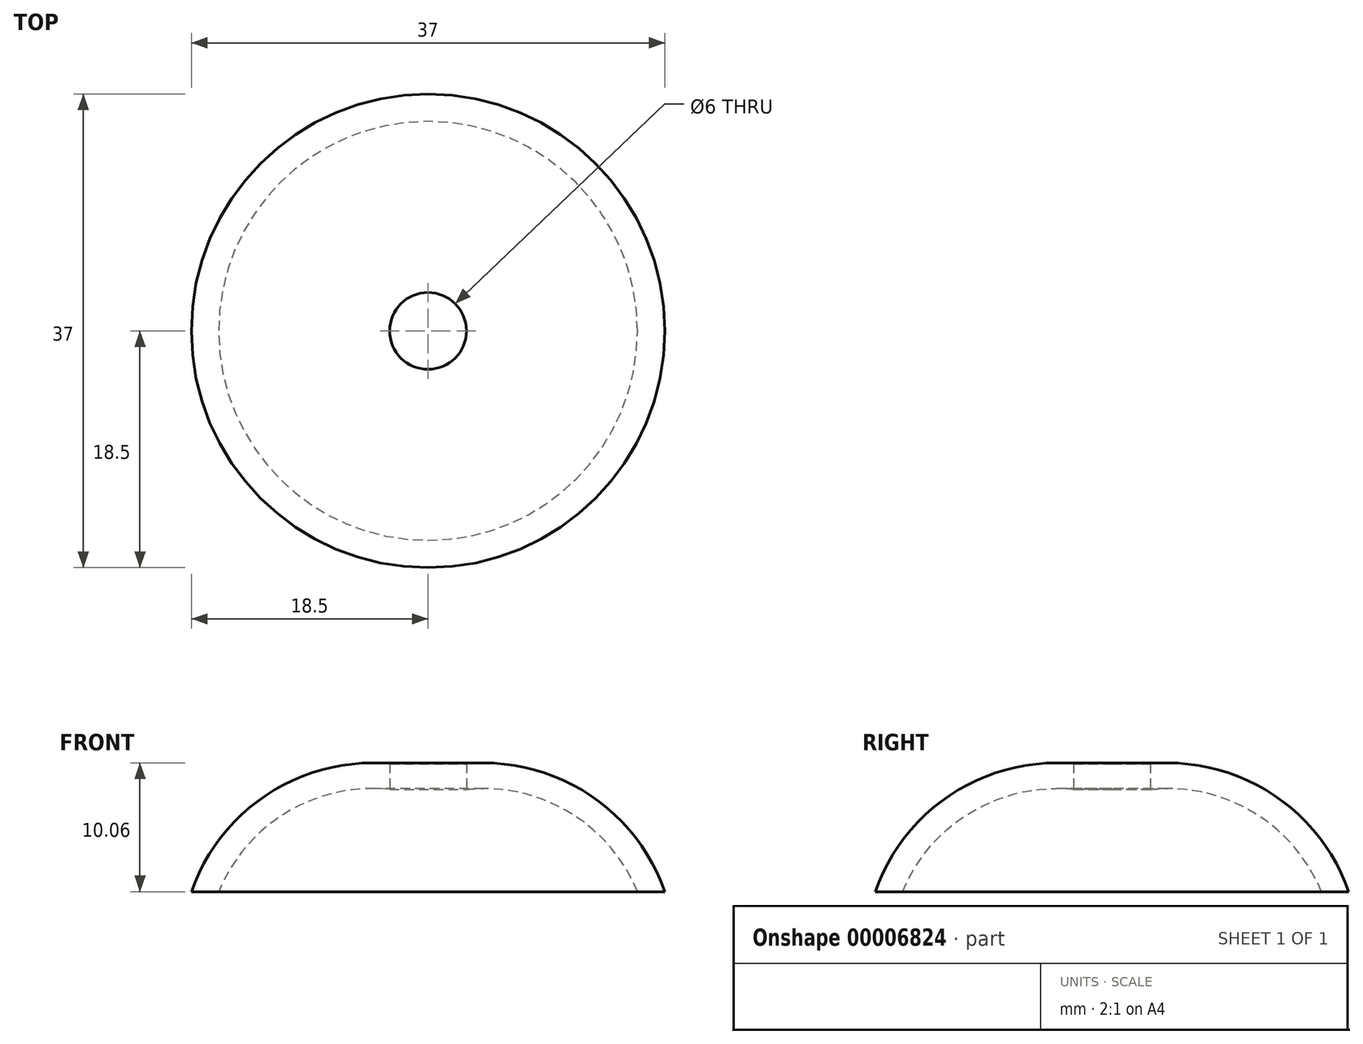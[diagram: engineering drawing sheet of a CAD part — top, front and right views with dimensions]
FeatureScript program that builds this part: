
annotation { "Feature Type Name" : "Feature", "Feature Type Description" : "" }
export const myFeature = defineFeature(function(context is Context, id is Id, definition is map)
    precondition{}
    {
        {
            var Q0;
            Q0=qCreatedBy(makeId("Right.planeOp"),FACE);
            var sketch = newSketch(context, id + "F0", { "sketchPlane" : qUnion([Q0])});
            skLineSegment(sketch, "E0", {"start": v(0, 0) * mm, "end": v(0, -3.09) * mm});
            skLineSegment(sketch, "E1", {"start": v(4.26, -9.53) * mm, "end": v(36, -23) * mm});
            skLineSegment(sketch, "E2", {"start": v(36, -23) * mm, "end": v(70, -23) * mm});
            skLineSegment(sketch, "E3", {"start": v(90, -3) * mm, "end": v(90, 47) * mm});
            skLineSegment(sketch, "E4", {"start": v(70, 67) * mm, "end": v(7, 67) * mm});
            skLineSegment(sketch, "E5", {"start": v(7, 67) * mm, "end": v(7, 45) * mm});
            skLineSegment(sketch, "E6", {"start": v(7, 45) * mm, "end": v(61, 45) * mm});
            skLineSegment(sketch, "E7", {"start": v(68, 38) * mm, "end": v(68, 4) * mm});
            skLineSegment(sketch, "E8", {"start": v(61, -3) * mm, "end": v(36, -3) * mm});
            skLineSegment(sketch, "E9", {"start": v(36, -3) * mm, "end": v(36, 0) * mm});
            skLineSegment(sketch, "E10", {"start": v(36, 0) * mm, "end": v(0, 0) * mm});
            skLineSegment(sketch, "E11", {"start": v(36, -23) * mm, "end": v(21.85, -23) * mm, "construction": true});
            skPoint(sketch, "E12.visualSharp", {"position": v(90, -23) * mm});
            skArc(sketch, "E12.filletArc", {"start": v(70, -23) * mm, "mid": v(84.14, -17.14) * mm, "end": v(90, -3) * mm});
            skPoint(sketch, "E13.visualSharp", {"position": v(90, 67) * mm});
            skArc(sketch, "E13.filletArc", {"start": v(90, 47) * mm, "mid": v(84.14, 61.14) * mm, "end": v(70, 67) * mm});
            skPoint(sketch, "E14.visualSharp", {"position": v(68, 45) * mm});
            skArc(sketch, "E14.filletArc", {"start": v(68, 38) * mm, "mid": v(65.95, 42.95) * mm, "end": v(61, 45) * mm});
            skPoint(sketch, "E15.visualSharp", {"position": v(68, -3) * mm});
            skArc(sketch, "E15.filletArc", {"start": v(61, -3) * mm, "mid": v(65.95, -0.95) * mm, "end": v(68, 4) * mm});
            skPoint(sketch, "E16.visualSharp", {"position": v(0, -7.72) * mm});
            skArc(sketch, "E16.filletArc", {"start": v(0, -3.09) * mm, "mid": v(1.16, -6.95) * mm, "end": v(4.26, -9.53) * mm});
            skSolve(sketch);
        }
        {
            var Q0;
            Q0=qSketchRegion(id+"F0",true);
            extrude(context, id + "F1", {"entities" : qUnion([Q0]), "endBound" : BoundingType.SYMMETRIC, "depth" : 20 * mm});
        }
        {
            var Q0;
            Q0=makeQuery(id+"F1.opExtrude","SWEPT_FACE",FACE,{"disambiguationData":[OSD([sQuery(id+"F0.wireOp",EDGE,"E6")])]});
            var sketch = newSketch(context, id + "F2", { "sketchPlane" : qUnion([Q0])});
            skCircle(sketch, "E17", {"center": v(0, -18) * mm, "radius": 11 * mm});
            skCircle(sketch, "E18", {"center": v(0, -18) * mm, "radius": 7 * mm});
            skSolve(sketch);
        }
        {
            var Q0;
            Q0=qSketchRegion(id+"F2",true);
            extrude(context, id + "F3", {"entities" : qUnion([Q0]), "operationType" : NewBodyOperationType.ADD, "oppositeDirection" : true, "depth" : 25 * mm});
        }
        {
            var Q0;
            Q0=makeQuery(id+"F3.boolean.opBoolean","SPLIT",FACE,{"disambiguationData":[TD([makeQuery(id+"F3.opExtrude","SWEPT_FACE",FACE,{"disambiguationData":[OSD([sQuery(id+"F2.wireOp",EDGE,"E18")])]})])],"derivedFrom":makeQuery(id+"F1.opExtrude","SWEPT_FACE",FACE,{"disambiguationData":[OSD([sQuery(id+"F0.wireOp",EDGE,"E4")])]})});
            var sketch = newSketch(context, id + "F4", { "sketchPlane" : qUnion([Q0])});
            skCircle(sketch, "E19.0", {"center": v(0, 18) * mm, "radius": 7 * mm});
            skSolve(sketch);
        }
        {
            var Q0;
            Q0=qSketchRegion(id+"F4",true);
            extrude(context, id + "F5", {"entities" : qUnion([Q0]), "operationType" : NewBodyOperationType.REMOVE, "oppositeDirection" : true, "depth" : 25 * mm});
        }
        {
            var Q0;
            {var subQ0=sQuery(id+"F0.wireOp",EDGE,"E4");var subQ1=makeQuery(id+"F1.opExtrude","SWEPT_FACE",FACE,{"disambiguationData":[OSD([subQ0])]});var subQ2=sQuery(id+"F0.wireOp",EDGE,"E5");Q0=makeQuery(id+"F3.boolean.opBoolean","SPLIT",FACE,{"disambiguationData":[TD([makeQuery(id+"F1.opExtrude","CAP_FACE",FACE,{"disambiguationData":[OSD([sQuery(id+"F0.wireOp",EDGE,"E0"),sQuery(id+"F0.wireOp",EDGE,"E1"),sQuery(id+"F0.wireOp",EDGE,"E2"),sQuery(id+"F0.wireOp",EDGE,"E3"),subQ0,subQ2,sQuery(id+"F0.wireOp",EDGE,"E6"),sQuery(id+"F0.wireOp",EDGE,"E7"),sQuery(id+"F0.wireOp",EDGE,"E8"),sQuery(id+"F0.wireOp",EDGE,"E9"),sQuery(id+"F0.wireOp",EDGE,"E10"),sQuery(id+"F0.wireOp",EDGE,"E12.filletArc"),sQuery(id+"F0.wireOp",EDGE,"E13.filletArc"),sQuery(id+"F0.wireOp",EDGE,"E14.filletArc"),sQuery(id+"F0.wireOp",EDGE,"E15.filletArc"),sQuery(id+"F0.wireOp",EDGE,"E16.filletArc")])],"isStart":false}),subQ1,makeQuery(id+"F1.opExtrude","SWEPT_FACE",FACE,{"disambiguationData":[OSD([subQ2])]}),makeQuery(id+"F3.opExtrude","SWEPT_FACE",FACE,{"disambiguationData":[OSD([sQuery(id+"F2.wireOp",EDGE,"E17")])]})])],"derivedFrom":subQ1});}
            var sketch = newSketch(context, id + "F6", { "sketchPlane" : qUnion([Q0])});
            skLineSegment(sketch, "E20.1.0", {"start": v(-10, 7) * mm, "end": v(0, 7) * mm});
            skArc(sketch, "E20.1.1", {"start": v(0, 7) * mm, "mid": v(-5.94, 8.74) * mm, "end": v(-10, 13.42) * mm});
            skLineSegment(sketch, "E20.1.2", {"start": v(-10, 13.42) * mm, "end": v(-10, 7) * mm});
            skSolve(sketch);
        }
        {
            var Q0;
            Q0=qSketchRegion(id+"F6",true);
            extrude(context, id + "F7", {"entities" : qUnion([Q0]), "operationType" : NewBodyOperationType.REMOVE, "oppositeDirection" : true, "depth" : 25 * mm});
        }
        {
            var Q0;
            {var subQ0=sQuery(id+"F0.wireOp",EDGE,"E4");var subQ1=makeQuery(id+"F1.opExtrude","SWEPT_FACE",FACE,{"disambiguationData":[OSD([subQ0])]});var subQ2=sQuery(id+"F0.wireOp",EDGE,"E5");Q0=makeQuery(id+"F3.boolean.opBoolean","SPLIT",FACE,{"disambiguationData":[TD([makeQuery(id+"F1.opExtrude","CAP_FACE",FACE,{"disambiguationData":[OSD([sQuery(id+"F0.wireOp",EDGE,"E0"),sQuery(id+"F0.wireOp",EDGE,"E1"),sQuery(id+"F0.wireOp",EDGE,"E2"),sQuery(id+"F0.wireOp",EDGE,"E3"),subQ0,subQ2,sQuery(id+"F0.wireOp",EDGE,"E6"),sQuery(id+"F0.wireOp",EDGE,"E7"),sQuery(id+"F0.wireOp",EDGE,"E8"),sQuery(id+"F0.wireOp",EDGE,"E9"),sQuery(id+"F0.wireOp",EDGE,"E10"),sQuery(id+"F0.wireOp",EDGE,"E12.filletArc"),sQuery(id+"F0.wireOp",EDGE,"E13.filletArc"),sQuery(id+"F0.wireOp",EDGE,"E14.filletArc"),sQuery(id+"F0.wireOp",EDGE,"E15.filletArc"),sQuery(id+"F0.wireOp",EDGE,"E16.filletArc")])],"isStart":false}),subQ1,makeQuery(id+"F1.opExtrude","SWEPT_FACE",FACE,{"disambiguationData":[OSD([subQ2])]}),makeQuery(id+"F3.opExtrude","SWEPT_FACE",FACE,{"disambiguationData":[OSD([sQuery(id+"F2.wireOp",EDGE,"E17")])]})])],"derivedFrom":subQ1});}
            var sketch = newSketch(context, id + "F8", { "sketchPlane" : qUnion([Q0])});
            skArc(sketch, "E21.0", {"start": v(10, 13.42) * mm, "mid": v(5.94, 8.74) * mm, "end": v(0, 7) * mm});
            skLineSegment(sketch, "E22", {"start": v(10, 13.42) * mm, "end": v(10, 7) * mm});
            skLineSegment(sketch, "E23", {"start": v(10, 7) * mm, "end": v(0, 7) * mm});
            skSolve(sketch);
        }
        {
            var Q0;
            Q0=qSketchRegion(id+"F8",true);
            extrude(context, id + "F9", {"entities" : qUnion([Q0]), "operationType" : NewBodyOperationType.REMOVE, "oppositeDirection" : true, "depth" : 25 * mm});
        }
        {
            var Q0;
            Q0=makeQuery(id+"F1.opExtrude","SWEPT_EDGE",EDGE,{"disambiguationData":[OSD([sQuery(id+"F0.wireOp",EDGE,"E8"),sQuery(id+"F0.wireOp",EDGE,"E9")])]});
            fillet(context, id + "F10", {"entities" : qUnion([Q0]), "radius" : 3 * mm, "tangentPropagation" : true, "allowEdgeOverflow" : false});
        }
        {
            var Q0;
            Q0=qCreatedBy(makeId("Right.planeOp"),FACE);
            var sketch = newSketch(context, id + "F11", { "sketchPlane" : qUnion([Q0])});
            skLineSegment(sketch, "E24", {"start": v(11, 100) * mm, "end": v(7, 100) * mm});
            skLineSegment(sketch, "E25", {"start": v(7, 100) * mm, "end": v(7, 118) * mm});
            skLineSegment(sketch, "E26", {"start": v(7, 118) * mm, "end": v(18, 118) * mm});
            skLineSegment(sketch, "E27", {"start": v(18, 118) * mm, "end": v(18, 35) * mm});
            skLineSegment(sketch, "E28", {"start": v(11, 100) * mm, "end": v(11, 35) * mm});
            skLineSegment(sketch, "E29", {"start": v(11, 35) * mm, "end": v(18, 35) * mm});
            skSolve(sketch);
        }
        {
            var Q0;
            Q0=qSketchRegion(id+"F11",true);
            var Q1;
            Q1=sQuery(id+"F11.wireOp",EDGE,"E27");
            revolve(context, id + "F12", {"entities" : qUnion([Q0]), "axis" : qUnion([Q1]), "revolveType" : RevolveType.FULL});
        }
        {
            var Q0;
            Q0=makeQuery(id+"F12.opRevolve","SWEPT_EDGE",EDGE,{"disambiguationData":[OSD([sQuery(id+"F11.wireOp",EDGE,"E25"),sQuery(id+"F11.wireOp",EDGE,"E26")])]});
            chamfer(context, id + "F13", {"entities" : qUnion([Q0]), "width" : 2 * mm, "tangentPropagation" : true});
        }
        {
            var Q0;
            Q0=makeQuery(id+"F12.opRevolve","SWEPT_FACE",FACE,{"disambiguationData":[OSD([sQuery(id+"F11.wireOp",EDGE,"E29")])]});
            var sketch = newSketch(context, id + "F14", { "sketchPlane" : qUnion([Q0])});
            skCircle(sketch, "E30", {"center": v(0, -18) * mm, "radius": 5 * mm});
            skSolve(sketch);
        }
        {
            var Q0;
            Q0=qSketchRegion(id+"F14",true);
            extrude(context, id + "F15", {"entities" : qUnion([Q0]), "operationType" : NewBodyOperationType.ADD, "depth" : 2 * mm});
        }
        {
            var Q0;
            Q0=makeQuery(id+"F15.opExtrude","CAP_FACE",FACE,{"disambiguationData":[OSD([sQuery(id+"F14.wireOp",EDGE,"E30")])],"isStart":false});
            var sketch = newSketch(context, id + "F16", { "sketchPlane" : qUnion([Q0])});
            skCircle(sketch, "E31", {"center": v(0, -18) * mm, "radius": 3 * mm});
            skSolve(sketch);
        }
        {
            var Q0;
            Q0=qSketchRegion(id+"F16",true);
            extrude(context, id + "F17", {"entities" : qUnion([Q0]), "operationType" : NewBodyOperationType.ADD, "depth" : 8 * mm});
        }
        {
            var Q0;
            Q0=qCreatedBy(makeId("Right.planeOp"),FACE);
            var sketch = newSketch(context, id + "F18", { "sketchPlane" : qUnion([Q0])});
            skCircle(sketch, "E32", {"center": v(18, 109) * mm, "radius": 5 * mm});
            skSolve(sketch);
        }
        {
            var Q0;
            Q0=qSketchRegion(id+"F18",true);
            extrude(context, id + "F19", {"entities" : qUnion([Q0]), "operationType" : NewBodyOperationType.REMOVE, "oppositeDirection" : true, "depth" : 25 * mm});
        }
        {
            var Q0;
            Q0=makeQuery(id+"F19.boolean.opBoolean","COPY",FACE,{"derivedFrom":makeQuery(id+"F19.opExtrude","CAP_FACE",FACE,{"disambiguationData":[OSD([sQuery(id+"F18.wireOp",EDGE,"E32")])],"isStart":true})});
            var sketch = newSketch(context, id + "F20", { "sketchPlane" : qUnion([Q0])});
            skCircle(sketch, "E33.0", {"center": v(-18, 109) * mm, "radius": 5 * mm});
            skSolve(sketch);
        }
        {
            var Q0;
            Q0=qSketchRegion(id+"F20",true);
            extrude(context, id + "F21", {"entities" : qUnion([Q0]), "operationType" : NewBodyOperationType.REMOVE, "oppositeDirection" : true, "depth" : 25 * mm});
        }
        {
            var Q0;
            Q0=qCreatedBy(makeId("Right.planeOp"),FACE);
            var sketch = newSketch(context, id + "F22", { "sketchPlane" : qUnion([Q0])});
            skCircle(sketch, "E34.0", {"center": v(18, 109) * mm, "radius": 5 * mm});
            skSolve(sketch);
        }
        {
            var Q0;
            Q0=qSketchRegion(id+"F22",true);
            extrude(context, id + "F23", {"entities" : qUnion([Q0]), "endBound" : BoundingType.SYMMETRIC, "depth" : 89 * mm});
        }
        {
            var Q0;
            Q0=makeQuery(id+"F23.opExtrude","CAP_FACE",FACE,{"disambiguationData":[OSD([sQuery(id+"F22.wireOp",EDGE,"E34.0")])],"isStart":false});
            var sketch = newSketch(context, id + "F24", { "sketchPlane" : qUnion([Q0])});
            skCircle(sketch, "E35", {"center": v(18, 109) * mm, "radius": 3 * mm});
            skSolve(sketch);
        }
        {
            var Q0;
            Q0=qSketchRegion(id+"F24",true);
            extrude(context, id + "F25", {"entities" : qUnion([Q0]), "operationType" : NewBodyOperationType.ADD, "depth" : 12 * mm});
        }
        {
            var Q0;
            Q0=makeQuery(id+"F23.opExtrude","CAP_FACE",FACE,{"disambiguationData":[OSD([sQuery(id+"F22.wireOp",EDGE,"E34.0")])],"isStart":true});
            var sketch = newSketch(context, id + "F26", { "sketchPlane" : qUnion([Q0])});
            skCircle(sketch, "E36", {"center": v(-18, 109) * mm, "radius": 3 * mm});
            skSolve(sketch);
        }
        {
            var Q0;
            Q0=qSketchRegion(id+"F26",true);
            extrude(context, id + "F27", {"entities" : qUnion([Q0]), "operationType" : NewBodyOperationType.ADD, "depth" : 12 * mm});
        }
        {
            var Q0;
            Q0=makeQuery(id+"F25.opExtrude","CAP_FACE",FACE,{"disambiguationData":[OSD([sQuery(id+"F24.wireOp",EDGE,"E35")])],"isStart":false});
            var sketch = newSketch(context, id + "F28", { "sketchPlane" : qUnion([Q0])});
            skCircle(sketch, "E37.0", {"center": v(18, 109) * mm, "radius": 3 * mm});
            skCircle(sketch, "E38", {"center": v(18, 109) * mm, "radius": 10 * mm});
            skSolve(sketch);
        }
        {
            var Q0;
            Q0=qSketchRegion(id+"F28",true);
            extrude(context, id + "F29", {"entities" : qUnion([Q0]), "oppositeDirection" : true, "depth" : 10 * mm});
        }
        {
            var Q0;
            Q0=makeQuery(id+"F29.opExtrude","CAP_EDGE",EDGE,{"disambiguationData":[OSD([sQuery(id+"F28.wireOp",EDGE,"E38")])],"isStart":true});
            var Q1;
            Q1=makeQuery(id+"F29.opExtrude","CAP_EDGE",EDGE,{"disambiguationData":[OSD([sQuery(id+"F28.wireOp",EDGE,"E38")])],"isStart":false});
            chamfer(context, id + "F30", {"entities" : qUnion([Q0, Q1]), "width" : 2 * mm, "tangentPropagation" : true});
        }
        {
            var Q0;
            Q0=makeQuery(id+"F29.opExtrude","SWEPT_BODY",BODY,{"disambiguationData":[OSD([sQuery(id+"F28.wireOp",EDGE,"E37.0"),sQuery(id+"F28.wireOp",EDGE,"E38")])]});
            var Q1;
            Q1=qCreatedBy(makeId("Right.planeOp"),FACE);
            mirror(context, id + "F31", {"entities" : qUnion([Q0]), "mirrorPlane" : qUnion([Q1])});
        }
        {
            var Q0;
            Q0=qCreatedBy(makeId("Right.planeOp"),FACE);
            var sketch = newSketch(context, id + "F32", { "sketchPlane" : qUnion([Q0])});
            skLineSegment(sketch, "E39", {"start": v(21, 30) * mm, "end": v(21, 32) * mm});
            skLineSegment(sketch, "E40", {"start": v(34.36, 22) * mm, "end": v(36.5, 22) * mm});
            skArc(sketch, "E41", {"start": v(36.5, 22) * mm, "mid": v(30.47, 29.67) * mm, "end": v(21, 32) * mm});
            skArc(sketch, "E42.0", {"start": v(34.36, 22) * mm, "mid": v(29, 28.23) * mm, "end": v(21, 30) * mm});
            skLineSegment(sketch, "E43", {"start": v(18, 24.98) * mm, "end": v(18, 32) * mm});
            skSolve(sketch);
        }
        {
            var Q0;
            Q0=qSketchRegion(id+"F32",true);
            var Q1;
            Q1=sQuery(id+"F32.wireOp",EDGE,"E43");
            revolve(context, id + "F33", {"entities" : qUnion([Q0]), "axis" : qUnion([Q1]), "revolveType" : RevolveType.FULL});
        }
        {
            var Q0;
            Q0=makeQuery(id+"F1.opExtrude","SWEPT_BODY",BODY,{"disambiguationData":[OSD([sQuery(id+"F0.wireOp",EDGE,"E0"),sQuery(id+"F0.wireOp",EDGE,"E1"),sQuery(id+"F0.wireOp",EDGE,"E2"),sQuery(id+"F0.wireOp",EDGE,"E3"),sQuery(id+"F0.wireOp",EDGE,"E4"),sQuery(id+"F0.wireOp",EDGE,"E5"),sQuery(id+"F0.wireOp",EDGE,"E6"),sQuery(id+"F0.wireOp",EDGE,"E7"),sQuery(id+"F0.wireOp",EDGE,"E8"),sQuery(id+"F0.wireOp",EDGE,"E9"),sQuery(id+"F0.wireOp",EDGE,"E10"),sQuery(id+"F0.wireOp",EDGE,"E12.filletArc"),sQuery(id+"F0.wireOp",EDGE,"E13.filletArc"),sQuery(id+"F0.wireOp",EDGE,"E14.filletArc"),sQuery(id+"F0.wireOp",EDGE,"E15.filletArc"),sQuery(id+"F0.wireOp",EDGE,"E16.filletArc")])]});
            deleteBodies(context, id + "F34", {"entities" : qUnion([Q0])});
        }
        {
            var Q0;
            Q0=makeQuery(id+"F12.opRevolve","SWEPT_BODY",BODY,{"disambiguationData":[OSD([sQuery(id+"F11.wireOp",EDGE,"E24"),sQuery(id+"F11.wireOp",EDGE,"E25"),sQuery(id+"F11.wireOp",EDGE,"E26"),sQuery(id+"F11.wireOp",EDGE,"E27"),sQuery(id+"F11.wireOp",EDGE,"E28"),sQuery(id+"F11.wireOp",EDGE,"E29")])]});
            deleteBodies(context, id + "F35", {"entities" : qUnion([Q0])});
        }
        {
            var Q0;
            Q0=makeQuery(id+"F23.opExtrude","SWEPT_BODY",BODY,{"disambiguationData":[OSD([sQuery(id+"F22.wireOp",EDGE,"E34.0")])]});
            deleteBodies(context, id + "F36", {"entities" : qUnion([Q0])});
        }
        {
            var Q0;
            Q0=makeQuery(id+"F31.opPattern","COPY",BODY,{"derivedFrom":makeQuery(id+"F29.opExtrude","SWEPT_BODY",BODY,{"disambiguationData":[OSD([sQuery(id+"F28.wireOp",EDGE,"E37.0"),sQuery(id+"F28.wireOp",EDGE,"E38")])]}),"instanceName":"1"});
            deleteBodies(context, id + "F37", {"entities" : qUnion([Q0])});
        }
        {
            var Q0;
            Q0=makeQuery(id+"F29.opExtrude","SWEPT_BODY",BODY,{"disambiguationData":[OSD([sQuery(id+"F28.wireOp",EDGE,"E37.0"),sQuery(id+"F28.wireOp",EDGE,"E38")])]});
            deleteBodies(context, id + "F38", {"entities" : qUnion([Q0])});
        }
    });
